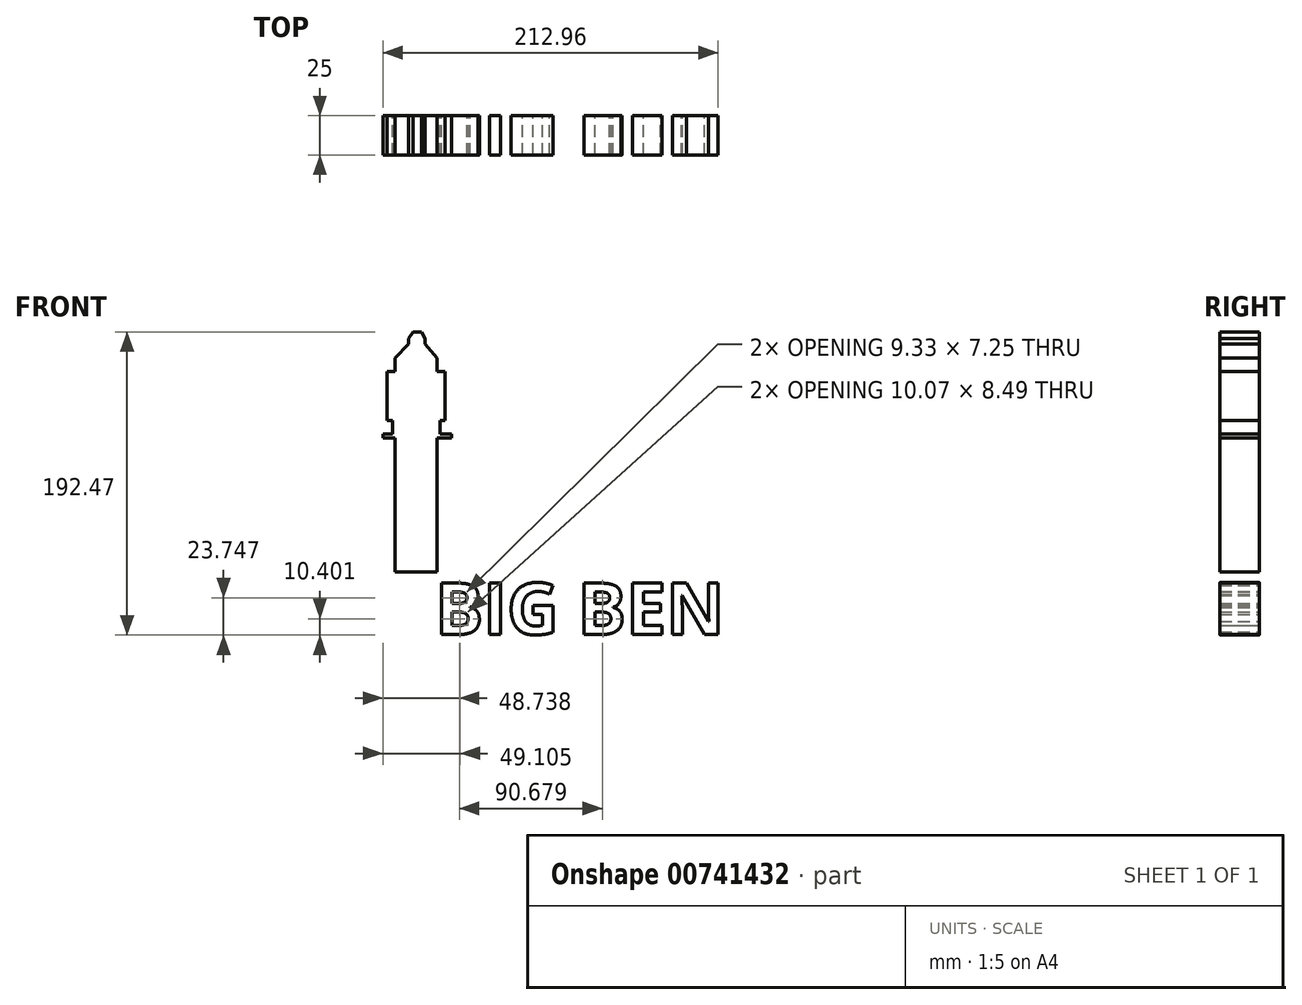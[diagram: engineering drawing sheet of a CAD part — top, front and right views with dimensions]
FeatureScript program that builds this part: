
annotation { "Feature Type Name" : "Feature", "Feature Type Description" : "" }
export const myFeature = defineFeature(function(context is Context, id is Id, definition is map)
    precondition{}
    {
        {
            var Q0;
            Q0=qCreatedBy(makeId("Front.planeOp"),FACE);
            var sketch = newSketch(context, id + "F0", { "sketchPlane" : qUnion([Q0])});
            skLineSegment(sketch, "E0.bottom", {"start": v(0, 0) * mm, "end": v(300, 0) * mm, "construction": true});
            skLineSegment(sketch, "E0.top", {"start": v(0, -200) * mm, "end": v(300, -200) * mm, "construction": true});
            skLineSegment(sketch, "E0.left", {"start": v(0, 0) * mm, "end": v(0, -200) * mm, "construction": true});
            skLineSegment(sketch, "E0.right", {"start": v(300, 0) * mm, "end": v(300, -200) * mm, "construction": true});
            skLineSegment(sketch, "E1", {"start": v(0, -152.23) * mm, "end": v(300, -152.23) * mm});
            skLineSegment(sketch, "E2", {"start": v(300, -152.23) * mm, "end": v(0, -152.23) * mm});
            skLineSegment(sketch, "E3", {"start": v(28.32, -152.23) * mm, "end": v(28.32, -67.43) * mm});
            skLineSegment(sketch, "E4", {"start": v(28.32, -67.43) * mm, "end": v(20.41, -67.43) * mm});
            skLineSegment(sketch, "E5", {"start": v(20.41, -67.43) * mm, "end": v(20.41, -64.75) * mm});
            skLineSegment(sketch, "E6", {"start": v(20.41, -64.75) * mm, "end": v(26.59, -64.75) * mm});
            skLineSegment(sketch, "E7", {"start": v(26.59, -64.75) * mm, "end": v(26.59, -56.3) * mm});
            skLineSegment(sketch, "E8", {"start": v(26.59, -56.3) * mm, "end": v(23.24, -56.3) * mm});
            skLineSegment(sketch, "E9", {"start": v(23.24, -56.3) * mm, "end": v(23.24, -25.2) * mm});
            skLineSegment(sketch, "E10", {"start": v(23.24, -25.2) * mm, "end": v(28.32, -25.2) * mm});
            skLineSegment(sketch, "E11", {"start": v(28.32, -25.2) * mm, "end": v(28.32, -16.33) * mm});
            skLineSegment(sketch, "E12", {"start": v(28.32, -16.33) * mm, "end": v(36.87, -7.53) * mm});
            skLineSegment(sketch, "E13", {"start": v(36.87, -7.53) * mm, "end": v(36.87, -4.04) * mm});
            skLineSegment(sketch, "E14", {"start": v(36.87, -4.04) * mm, "end": v(39.45, 0) * mm});
            skLineSegment(sketch, "E15", {"start": v(39.45, 0) * mm, "end": v(45.06, 0) * mm});
            skLineSegment(sketch, "E16", {"start": v(45.06, 0) * mm, "end": v(47.18, -4.04) * mm});
            skLineSegment(sketch, "E17", {"start": v(47.18, -4.04) * mm, "end": v(47.18, -7.53) * mm});
            skLineSegment(sketch, "E18", {"start": v(47.18, -7.53) * mm, "end": v(54.91, -16.33) * mm});
            skLineSegment(sketch, "E19", {"start": v(54.91, -16.33) * mm, "end": v(54.91, -25.2) * mm});
            skLineSegment(sketch, "E20", {"start": v(54.91, -25.2) * mm, "end": v(59.77, -25.2) * mm});
            skLineSegment(sketch, "E21", {"start": v(59.77, -25.2) * mm, "end": v(59.77, -56.3) * mm});
            skLineSegment(sketch, "E22", {"start": v(59.77, -56.3) * mm, "end": v(56.58, -56.3) * mm});
            skLineSegment(sketch, "E23", {"start": v(56.58, -56.3) * mm, "end": v(56.58, -64.75) * mm});
            skLineSegment(sketch, "E24", {"start": v(56.58, -64.75) * mm, "end": v(64.01, -64.75) * mm});
            skLineSegment(sketch, "E25", {"start": v(64.01, -64.75) * mm, "end": v(64.01, -67.43) * mm});
            skLineSegment(sketch, "E26", {"start": v(64.01, -67.43) * mm, "end": v(54.91, -67.43) * mm});
            skLineSegment(sketch, "E27", {"start": v(54.91, -67.43) * mm, "end": v(54.91, -152.23) * mm});
            skText(sketch, "E28", { "text": "BIG BEN ", "fontName": "OpenSans-Bold.ttf"});
            const initialGuessF0  = {"E28": [0.05347, -0.19202, 1, 0, 0.03286]};
            skSetInitialGuess(sketch, initialGuessF0);
            skSolve(sketch);
        }
        {
            var Q0;
            Q0 = qSketchRegion(id + "F0", true);
            extrude(context, id + "F1", {"entities" : qUnion([Q0]), "depth" : 25 * mm, "offsetDistance" : 25 * mm});
        }
    });
